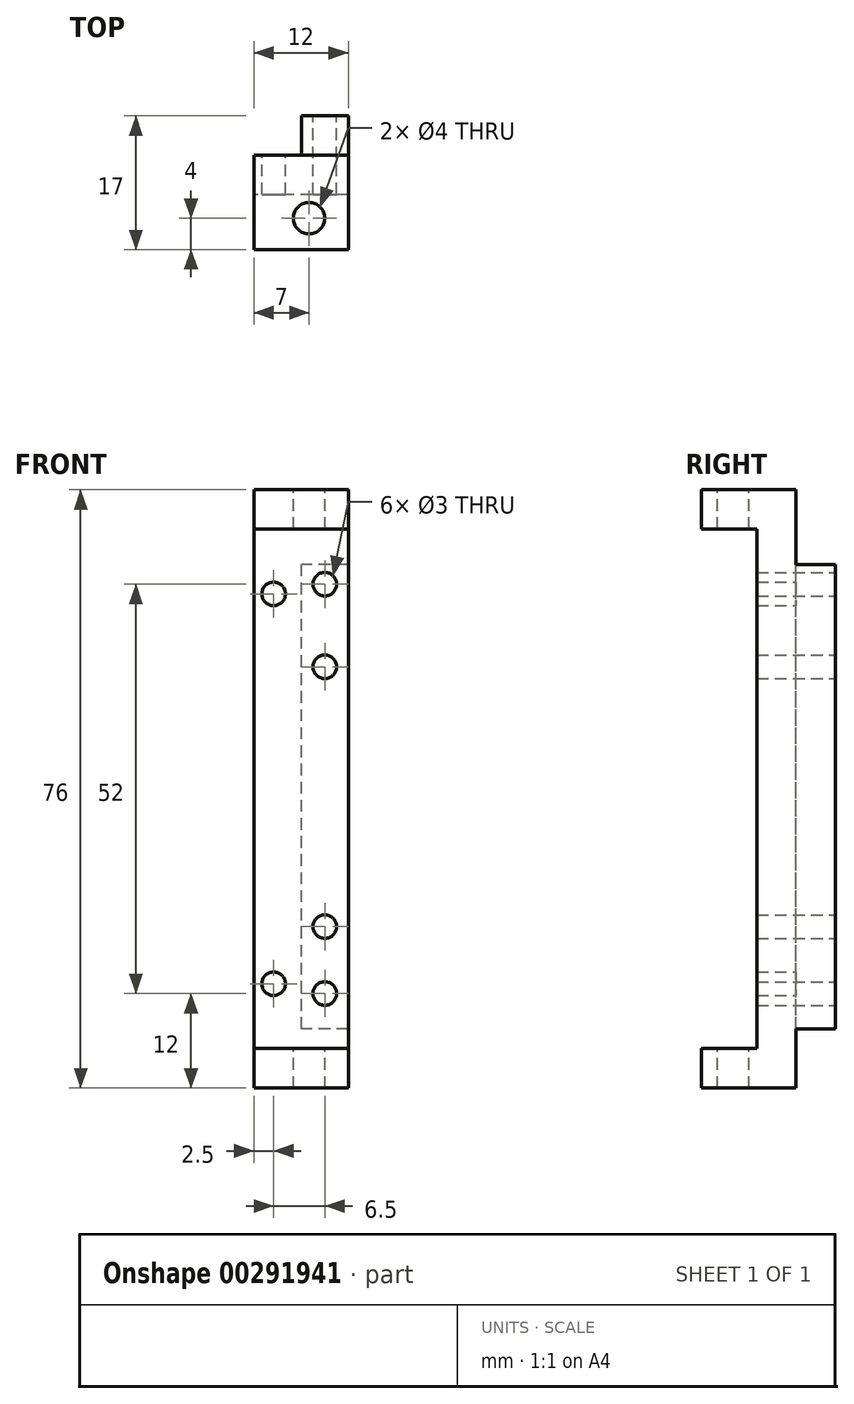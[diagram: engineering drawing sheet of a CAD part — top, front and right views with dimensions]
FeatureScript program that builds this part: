
annotation { "Feature Type Name" : "Feature", "Feature Type Description" : "" }
export const myFeature = defineFeature(function(context is Context, id is Id, definition is map)
    precondition{}
    {
        {
            var Q0;
            Q0=qCreatedBy(makeId("Right.planeOp"),FACE);
            var sketch = newSketch(context, id + "F0", { "sketchPlane" : qUnion([Q0])});
            skLineSegment(sketch, "E0", {"start": v(-3.5, 40.5) * mm, "end": v(13.5, 40.5) * mm});
            skLineSegment(sketch, "E1", {"start": v(13.5, 40.5) * mm, "end": v(13.5, -35.5) * mm});
            skLineSegment(sketch, "E2.0", {"start": v(3.5, 35.5) * mm, "end": v(3.5, -35.5) * mm});
            skLineSegment(sketch, "E2.1", {"start": v(-3.5, 35.5) * mm, "end": v(3.5, 35.5) * mm});
            skLineSegment(sketch, "E3", {"start": v(-3.5, 40.5) * mm, "end": v(-3.5, 35.5) * mm});
            skLineSegment(sketch, "E4", {"start": v(13.5, -35.5) * mm, "end": v(3.5, -35.5) * mm});
            skLineSegment(sketch, "E5", {"start": v(3.5, 0) * mm, "end": v(-14.36, 0) * mm, "construction": true});
            skLineSegment(sketch, "E6", {"start": v(0, 35.5) * mm, "end": v(0, -1.72) * mm, "construction": true});
            skSolve(sketch);
        }
        {
            var Q0;
            Q0=makeQuery(id+"F0.imprint","IMPRINT",FACE,{"disambiguationData":[TD([[makeQuery(id+"F0.imprint","IMPRINT",EDGE,{"derivedFrom":sQuery(id+"F0.wireOp",EDGE,"E0")}),-1.0]])]});
            extrude(context, id + "F1", {"entities" : qUnion([Q0]), "depth" : 12 * mm});
        }
        {
            var Q0;
            Q0=makeQuery(id+"F1.opExtrude","SWEPT_FACE",FACE,{"disambiguationData":[OSD([sQuery(id+"F0.wireOp",EDGE,"E0")])]});
            var sketch = newSketch(context, id + "F2", { "sketchPlane" : qUnion([Q0])});
            skLineSegment(sketch, "E7.bottom", {"start": v(0, 13.5) * mm, "end": v(6.02, 13.5) * mm});
            skLineSegment(sketch, "E7.top", {"start": v(0, 8.5) * mm, "end": v(6.02, 8.5) * mm});
            skLineSegment(sketch, "E7.left", {"start": v(0, 13.5) * mm, "end": v(0, 8.5) * mm});
            skLineSegment(sketch, "E7.right", {"start": v(6.02, 13.5) * mm, "end": v(6.02, 8.5) * mm});
            skSolve(sketch);
        }
        {
            var Q0;
            Q0=makeQuery(id+"F2.imprint","IMPRINT",FACE,{"disambiguationData":[TD([[makeQuery(id+"F2.imprint","IMPRINT",EDGE,{"derivedFrom":sQuery(id+"F2.wireOp",EDGE,"E7.bottom")}),1.0]])]});
            extrude(context, id + "F3", {"entities" : qUnion([Q0]), "operationType" : NewBodyOperationType.REMOVE, "oppositeDirection" : true, "depth" : 76 * mm});
        }
        {
            var Q0;
            Q0=makeQuery(id+"F1.opExtrude","SWEPT_FACE",FACE,{"disambiguationData":[OSD([sQuery(id+"F0.wireOp",EDGE,"E1")])]});
            var sketch = newSketch(context, id + "F4", { "sketchPlane" : qUnion([Q0])});
            skCircle(sketch, "E8", {"center": v(-9, 28.5) * mm, "radius": 1.5 * mm});
            skCircle(sketch, "E9", {"center": v(-9, -23.5) * mm, "radius": 1.5 * mm});
            skLineSegment(sketch, "E10", {"start": v(-9, 28.5) * mm, "end": v(-9, -23.5) * mm, "construction": true});
            skPoint(sketch, "E11", {"position": v(-9, 37.5) * mm});
            skLineSegment(sketch, "E12", {"start": v(-9, 28.5) * mm, "end": v(-9, 40.5) * mm, "construction": true});
            skSolve(sketch);
        }
        {
            var Q0;
            Q0=makeQuery(id+"F4.imprint","IMPRINT",FACE,{"disambiguationData":[TD([[makeQuery(id+"F4.imprint","IMPRINT",EDGE,{"derivedFrom":sQuery(id+"F4.wireOp",EDGE,"E8")}),1.0]])]});
            var Q1;
            Q1=makeQuery(id+"F4.imprint","IMPRINT",FACE,{"disambiguationData":[TD([[makeQuery(id+"F4.imprint","IMPRINT",EDGE,{"derivedFrom":sQuery(id+"F4.wireOp",EDGE,"E9")}),1.0]])]});
            extrude(context, id + "F5", {"entities" : qUnion([Q0, Q1]), "operationType" : NewBodyOperationType.REMOVE, "oppositeDirection" : true, "depth" : 25 * mm});
        }
        {
            var Q0;
            Q0=makeQuery(id+"F3.boolean.opBoolean","COPY",FACE,{"derivedFrom":makeQuery(id+"F3.opExtrude","SWEPT_FACE",FACE,{"disambiguationData":[OSD([sQuery(id+"F2.wireOp",EDGE,"E7.top")])]})});
            var sketch = newSketch(context, id + "F6", { "sketchPlane" : qUnion([Q0])});
            skCircle(sketch, "E13", {"center": v(-2.5, 27.26) * mm, "radius": 1.5 * mm});
            skCircle(sketch, "E14", {"center": v(-2.5, -22.27) * mm, "radius": 1.5 * mm});
            skLineSegment(sketch, "E15", {"start": v(-2.5, 27.26) * mm, "end": v(-2.5, -22.27) * mm, "construction": true});
            skSolve(sketch);
        }
        {
            var Q0;
            Q0=makeQuery(id+"F6.imprint","IMPRINT",FACE,{"disambiguationData":[TD([[makeQuery(id+"F6.imprint","IMPRINT",EDGE,{"derivedFrom":sQuery(id+"F6.wireOp",EDGE,"E14")}),1.0]])]});
            var Q1;
            Q1=makeQuery(id+"F6.imprint","IMPRINT",FACE,{"disambiguationData":[TD([[makeQuery(id+"F6.imprint","IMPRINT",EDGE,{"derivedFrom":sQuery(id+"F6.wireOp",EDGE,"E13")}),1.0]])]});
            extrude(context, id + "F7", {"entities" : qUnion([Q0, Q1]), "operationType" : NewBodyOperationType.REMOVE, "oppositeDirection" : true, "depth" : 25 * mm});
        }
        {
            var Q0;
            Q0=makeQuery(id+"F1.opExtrude","SWEPT_FACE",FACE,{"disambiguationData":[OSD([sQuery(id+"F0.wireOp",EDGE,"E2.0")])]});
            var sketch = newSketch(context, id + "F8", { "sketchPlane" : qUnion([Q0])});
            skLineSegment(sketch, "E16.bottom", {"start": v(0, -35.5) * mm, "end": v(12, -35.5) * mm});
            skLineSegment(sketch, "E16.top", {"start": v(0, -30.5) * mm, "end": v(12, -30.5) * mm});
            skLineSegment(sketch, "E16.left", {"start": v(0, -30.5) * mm, "end": v(0, -35.5) * mm});
            skLineSegment(sketch, "E16.right", {"start": v(12, -30.5) * mm, "end": v(12, -35.5) * mm});
            skSolve(sketch);
        }
        {
            var Q0;
            Q0=makeQuery(id+"F8.imprint","IMPRINT",FACE,{"disambiguationData":[TD([[makeQuery(id+"F8.imprint","IMPRINT",EDGE,{"derivedFrom":sQuery(id+"F8.wireOp",EDGE,"E16.bottom")}),-1.0]])]});
            extrude(context, id + "F9", {"entities" : qUnion([Q0]), "operationType" : NewBodyOperationType.ADD, "depth" : 7 * mm});
        }
        {
            var Q0;
            Q0=makeQuery(id+"F1.opExtrude","SWEPT_FACE",FACE,{"disambiguationData":[OSD([sQuery(id+"F0.wireOp",EDGE,"E0")])]});
            var sketch = newSketch(context, id + "F10", { "sketchPlane" : qUnion([Q0])});
            skCircle(sketch, "E17", {"center": v(7, 0.5) * mm, "radius": 2 * mm});
            skSolve(sketch);
        }
        {
            var Q0;
            Q0=makeQuery(id+"F10.imprint","IMPRINT",FACE,{"disambiguationData":[TD([[makeQuery(id+"F10.imprint","IMPRINT",EDGE,{"derivedFrom":sQuery(id+"F10.wireOp",EDGE,"3cef3784-0546-473a-8e1b-046f94c164f3")}),1.0]])]});
            var Q1;
            Q1=makeQuery(id+"F10.imprint","IMPRINT",FACE,{"disambiguationData":[TD([[makeQuery(id+"F10.imprint","IMPRINT",EDGE,{"derivedFrom":sQuery(id+"F10.wireOp",EDGE,"E17")}),1.0]])]});
            extrude(context, id + "F11", {"entities" : qUnion([Q0, Q1]), "operationType" : NewBodyOperationType.REMOVE, "oppositeDirection" : true, "depth" : 76 * mm});
        }
        {
            var Q0;
            Q0=makeQuery(id+"F1.opExtrude","SWEPT_FACE",FACE,{"disambiguationData":[OSD([sQuery(id+"F0.wireOp",EDGE,"E1")])]});
            var sketch = newSketch(context, id + "F12", { "sketchPlane" : qUnion([Q0])});
            skLineSegment(sketch, "E18.bottom", {"start": v(-12, 40.5) * mm, "end": v(-6.02, 40.5) * mm});
            skLineSegment(sketch, "E18.top", {"start": v(-12, 31) * mm, "end": v(-6.02, 31) * mm});
            skLineSegment(sketch, "E18.left", {"start": v(-12, 40.5) * mm, "end": v(-12, 31) * mm});
            skLineSegment(sketch, "E18.right", {"start": v(-6.02, 40.5) * mm, "end": v(-6.02, 31) * mm});
            skLineSegment(sketch, "E19.bottom", {"start": v(-12, -35.5) * mm, "end": v(-6.02, -35.5) * mm});
            skLineSegment(sketch, "E19.top", {"start": v(-12, -28) * mm, "end": v(-6.02, -28) * mm});
            skLineSegment(sketch, "E19.left", {"start": v(-12, -35.5) * mm, "end": v(-12, -28) * mm});
            skLineSegment(sketch, "E19.right", {"start": v(-6.02, -35.5) * mm, "end": v(-6.02, -28) * mm});
            skSolve(sketch);
        }
        {
            var Q0;
            Q0=qSketchRegion(id+"F12",true);
            extrude(context, id + "F13", {"entities" : qUnion([Q0]), "operationType" : NewBodyOperationType.REMOVE, "oppositeDirection" : true, "depth" : 5 * mm});
        }
        {
            var Q0;
            Q0=makeQuery(id+"F1.opExtrude","SWEPT_FACE",FACE,{"disambiguationData":[OSD([sQuery(id+"F0.wireOp",EDGE,"E1")])]});
            var sketch = newSketch(context, id + "F14", { "sketchPlane" : qUnion([Q0])});
            skCircle(sketch, "E20", {"center": v(-9, -15) * mm, "radius": 1.5 * mm});
            skCircle(sketch, "E21", {"center": v(-9, 18) * mm, "radius": 1.5 * mm});
            skLineSegment(sketch, "E22", {"start": v(-9, 18) * mm, "end": v(-9, -15) * mm, "construction": true});
            skSolve(sketch);
        }
        {
            var Q0;
            Q0=qSketchRegion(id+"F14",true);
            extrude(context, id + "F15", {"entities" : qUnion([Q0]), "operationType" : NewBodyOperationType.REMOVE, "oppositeDirection" : true, "depth" : 25 * mm});
        }
    });
